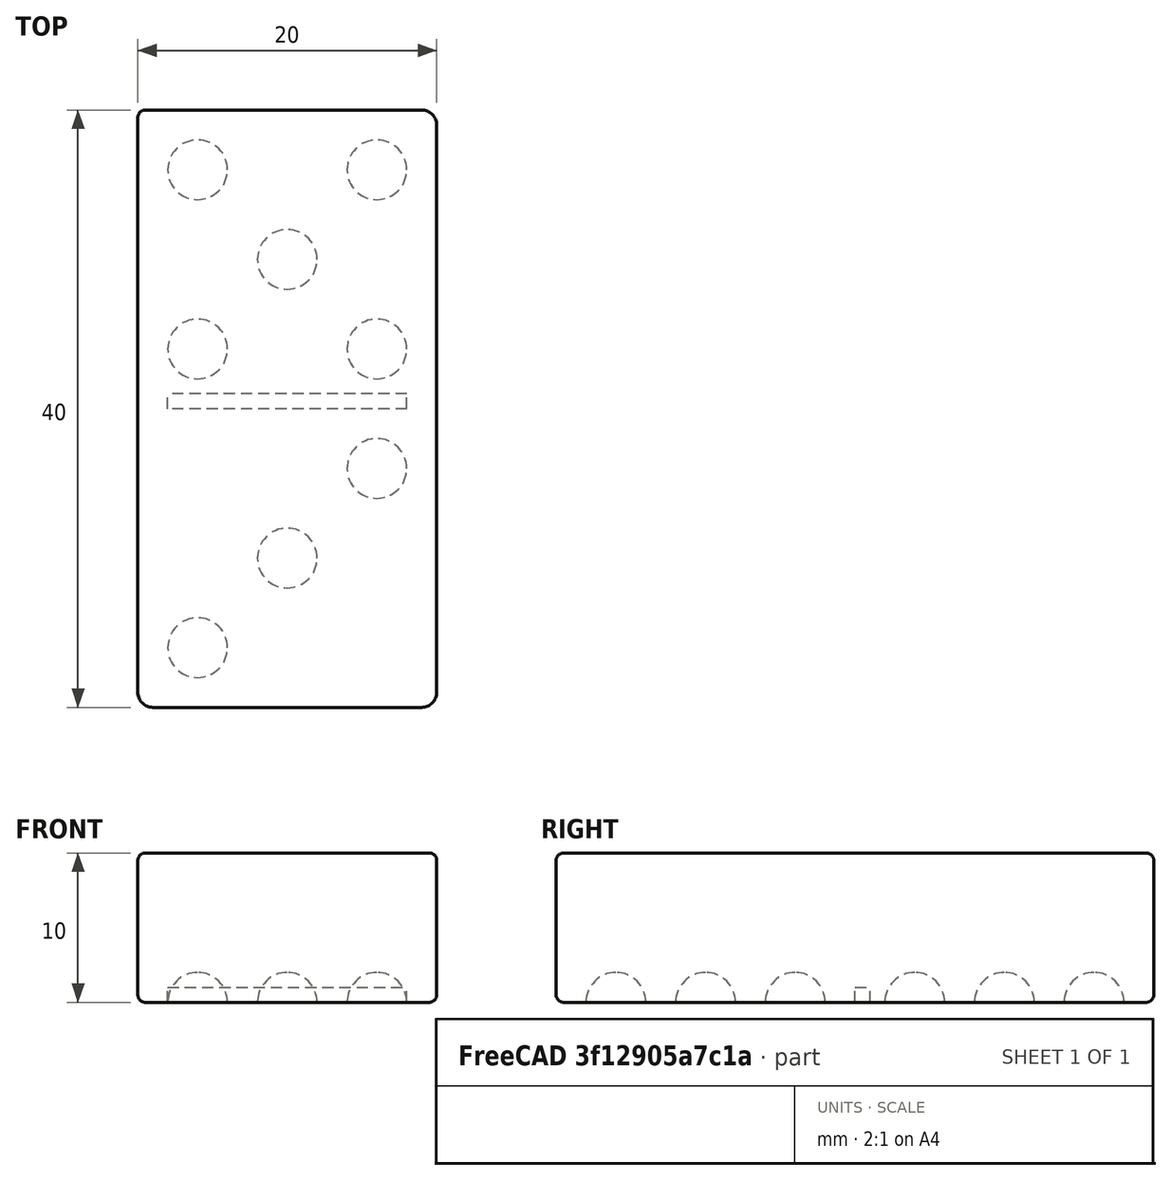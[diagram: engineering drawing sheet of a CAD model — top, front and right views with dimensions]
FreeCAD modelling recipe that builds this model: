
FCSTD DOCUMENT  (FreeCAD 1.0R39319 (Git))
Label: ojt1_t13p02_domino
License: All rights reserved
LicenseURL: https://en.wikipedia.org/wiki/All_rights_reserved
objects: Part::Sphere×8, Part::Box×2, Part::MultiFuse×1, Part::Cut×1, Part::Fillet×1
note: 13 computed .brp shape members not serialized (recipe doc carries the construction recipe); baked Part::Feature solids carry a one-line shape summary decoded from their .brp

FEATURE [Part::Box] Box  label="Cub"
  AttacherType = Attacher::AttachEngine3D
  Height = 10
  Length = 20
  Width = 40
FEATURE [Part::Sphere] Sphere  label="Esfera"
  Angle1 = -90
  Angle2 = 90
  Angle3 = 360
  AttacherType = Attacher::AttachEngine3D
  Placement = pos=(4,4,0) rot=(0,0,1;0rad)
  Radius = 2
FEATURE [Part::Sphere] Sphere001  label="Esfera001"
  Angle1 = -90
  Angle2 = 90
  Angle3 = 360
  AttacherType = Attacher::AttachEngine3D
  Placement = pos=(10,10,0) rot=(0,0,1;0rad)
  Radius = 2
FEATURE [Part::Sphere] Sphere002  label="Esfera002"
  Angle1 = -90
  Angle2 = 90
  Angle3 = 360
  AttacherType = Attacher::AttachEngine3D
  Placement = pos=(16,16,0) rot=(0,0,1;0rad)
  Radius = 2
FEATURE [Part::Sphere] Sphere003  label="Esfera003"
  Angle1 = -90
  Angle2 = 90
  Angle3 = 360
  AttacherType = Attacher::AttachEngine3D
  Placement = pos=(4,36,0) rot=(0,0,1;0rad)
  Radius = 2
FEATURE [Part::Sphere] Sphere004  label="Esfera004"
  Angle1 = -90
  Angle2 = 90
  Angle3 = 360
  AttacherType = Attacher::AttachEngine3D
  Placement = pos=(4,24,0) rot=(0,0,1;0rad)
  Radius = 2
FEATURE [Part::Sphere] Sphere005  label="Esfera005"
  Angle1 = -90
  Angle2 = 90
  Angle3 = 360
  AttacherType = Attacher::AttachEngine3D
  Placement = pos=(16,24,0) rot=(0,0,1;0rad)
  Radius = 2
FEATURE [Part::Sphere] Sphere006  label="Esfera006"
  Angle1 = -90
  Angle2 = 90
  Angle3 = 360
  AttacherType = Attacher::AttachEngine3D
  Placement = pos=(16,36,0) rot=(0,0,1;0rad)
  Radius = 2
FEATURE [Part::Sphere] Sphere007  label="Esfera007"
  Angle1 = -90
  Angle2 = 90
  Angle3 = 360
  AttacherType = Attacher::AttachEngine3D
  Placement = pos=(10,30,0) rot=(0,0,1;0rad)
  Radius = 2
FEATURE [Part::Box] Box001  label="Cub001"
  AttacherType = Attacher::AttachEngine3D
  Height = 10
  Length = 16
  Placement = pos=(2,20,-9) rot=(0,0,1;0rad)
  Width = 1
FEATURE [Part::MultiFuse] Fusion
  Shapes = -> [Sphere007,Box001,Sphere006,Sphere005,Sphere004,Sphere003,Sphere002,Sphere001,Sphere]
FEATURE [Part::Cut] Cut
  Base = -> Box
  Tool = -> Fusion
FEATURE [Part::Fillet] Fillet
  Base = -> Cut
  EdgeLinks = -> Cut [Edge1,Edge2,Edge3,Edge4,Edge5,Edge6,Edge7,Edge8,Edge9,Edge10,Edge11,Edge12]
  Edges = 12 edges: [Edge1 r=1,Edge2 r=0.5,Edge3 r=0.5,Edge4 r=0.5,Edge5 r=0.5,Edge6 r=1,Edge7 r=0.5,Edge8 r=0.5,Edge9 r=0.5,Edge10 r=0.5,Edge11 r=1,Edge12 r=0.5]
